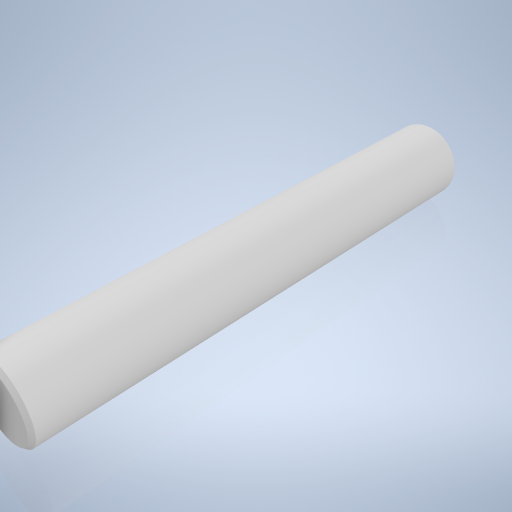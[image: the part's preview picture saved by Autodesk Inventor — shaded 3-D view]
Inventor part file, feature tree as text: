
AUTODESK INVENTOR PART (.ipt)
format: ipt  version: 2024.2 (Build 282272000, 272)  size: 230,400 bytes
history: native  units: mm
features: extrude x1, chamfer x1, sketch x1
ambient origin geometry x8: Origin, YZ Plane, XZ Plane, XY Plane, X Axis, Y Axis, Z Axis, Center Point
bodies: Volumenkörper1 (feature_tree)
feature tree (3):
  extrude  "Extrusion1"  Depth=13.0mm TaperAngle=0.0deg
  chamfer  "Fasen1"  Distance=0.1mm Angle=45.0deg
  sketch  "Skizze1"  dims[d0=2.0mm d1=13.0mm d2=0.0mm d3=0.1mm d4=2.0mm d5=45.0deg]
